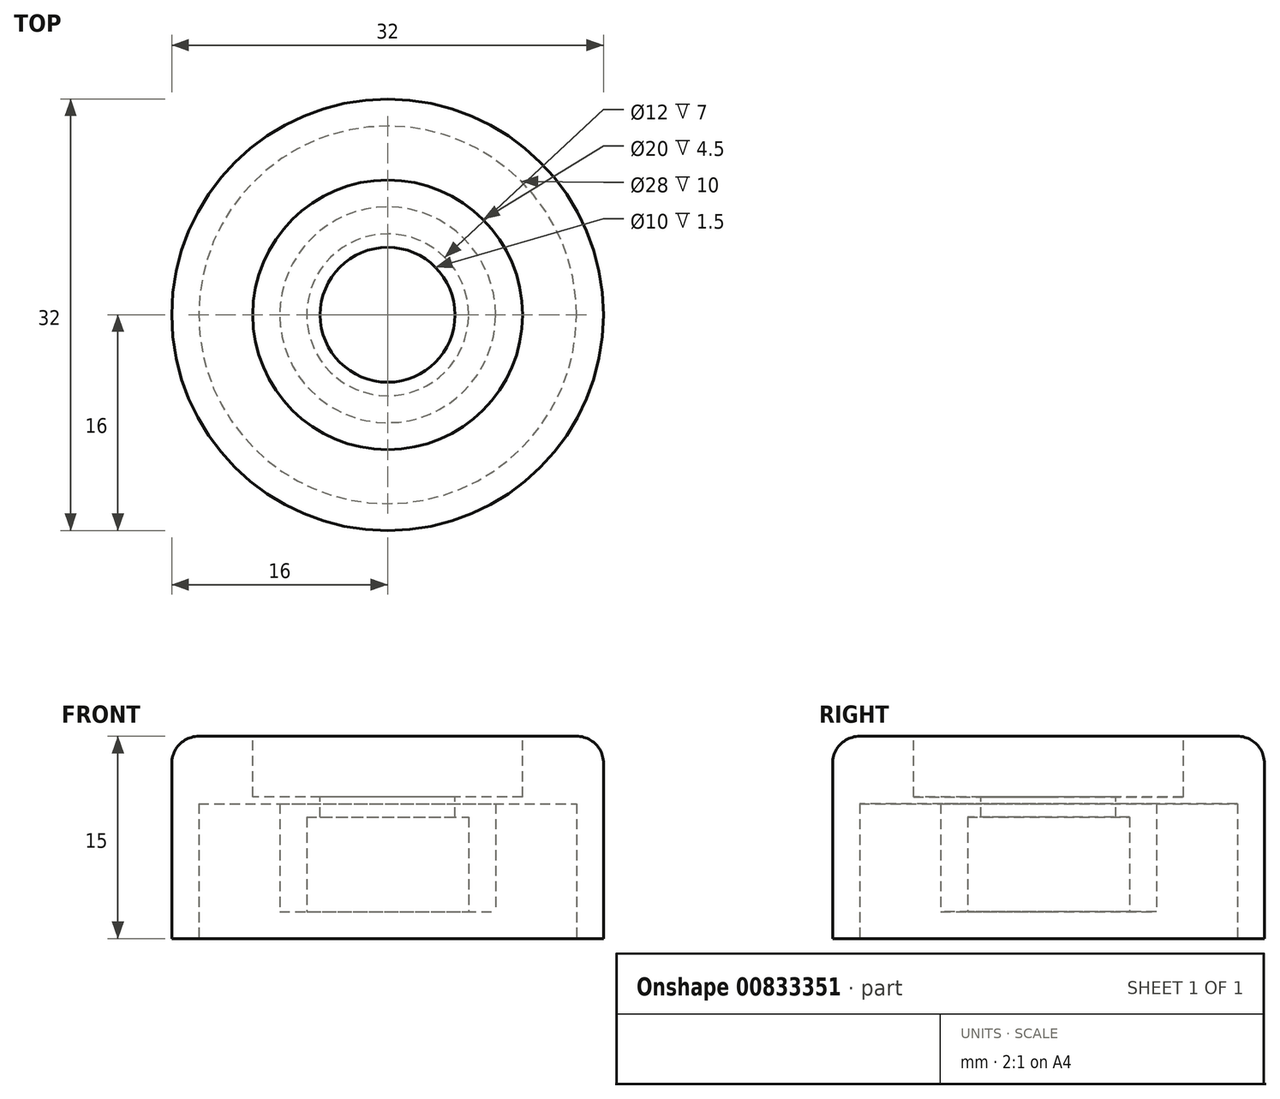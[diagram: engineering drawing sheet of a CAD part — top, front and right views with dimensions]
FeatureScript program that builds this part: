
annotation { "Feature Type Name" : "Feature", "Feature Type Description" : "" }
export const myFeature = defineFeature(function(context is Context, id is Id, definition is map)
    precondition{}
    {
        {
            var Q0;
            Q0=qCreatedBy(makeId("Top.planeOp"),FACE);
            var sketch = newSketch(context, id + "F0", { "sketchPlane" : qUnion([Q0])});
            skCircle(sketch, "E0", {"center": v(0, 0) * mm, "radius": 16 * mm});
            skSolve(sketch);
        }
        {
            var Q0;
            Q0=makeQuery(id+"F0.imprint","IMPRINT",FACE,{"disambiguationData":[TD([[makeQuery(id+"F0.imprint","IMPRINT",EDGE,{"derivedFrom":sQuery(id+"F0.wireOp",EDGE,"E0")}),1.0]])]});
            extrude(context, id + "F1", {"entities" : qUnion([Q0]), "depth" : 15 * mm, "offsetDistance" : 25 * mm});
        }
        {
            var Q0;
            Q0=makeQuery(id+"F1.opExtrude","CAP_FACE",FACE,{"disambiguationData":[OSD([sQuery(id+"F0.wireOp",EDGE,"E0")])],"isStart":false});
            var sketch = newSketch(context, id + "F2", { "sketchPlane" : qUnion([Q0])});
            skCircle(sketch, "E1", {"center": v(0, 0) * mm, "radius": 10 * mm});
            skSolve(sketch);
        }
        {
            var Q0;
            Q0=makeQuery(id+"F2.imprint","IMPRINT",FACE,{"disambiguationData":[TD([[makeQuery(id+"F2.imprint","IMPRINT",EDGE,{"derivedFrom":sQuery(id+"F2.wireOp",EDGE,"E1")}),1.0]])]});
            extrude(context, id + "F3", {"entities" : qUnion([Q0]), "operationType" : NewBodyOperationType.REMOVE, "oppositeDirection" : true, "depth" : 4.5 * mm, "offsetDistance" : 25 * mm});
        }
        {
            var Q0;
            Q0=makeQuery(id+"F1.opExtrude","CAP_FACE",FACE,{"disambiguationData":[OSD([sQuery(id+"F0.wireOp",EDGE,"E0")])],"isStart":true});
            var sketch = newSketch(context, id + "F4", { "sketchPlane" : qUnion([Q0])});
            skCircle(sketch, "E2", {"center": v(0, 0) * mm, "radius": 14 * mm});
            skCircle(sketch, "E3", {"center": v(0, 0) * mm, "radius": 6 * mm});
            skCircle(sketch, "E4", {"center": v(0, 0) * mm, "radius": 8 * mm});
            skSolve(sketch);
        }
        {
            var Q0;
            Q0=makeQuery(id+"F4.imprint","IMPRINT",FACE,{"disambiguationData":[TD([[makeQuery(id+"F4.imprint","IMPRINT",EDGE,{"derivedFrom":sQuery(id+"F4.wireOp",EDGE,"E2")}),1.0]])]});
            extrude(context, id + "F5", {"entities" : qUnion([Q0]), "operationType" : NewBodyOperationType.REMOVE, "oppositeDirection" : true, "depth" : 10 * mm, "offsetDistance" : 25 * mm});
        }
        {
            var Q0;
            Q0=makeQuery(id+"F5.boolean.opBoolean","SPLIT",FACE,{"disambiguationData":[TD([makeQuery(id+"F5.opExtrude","SWEPT_FACE",FACE,{"disambiguationData":[OSD([sQuery(id+"F4.wireOp",EDGE,"E4")])]})])],"derivedFrom":makeQuery(id+"F1.opExtrude","CAP_FACE",FACE,{"disambiguationData":[OSD([sQuery(id+"F0.wireOp",EDGE,"E0")])],"isStart":true})});
            var sketch = newSketch(context, id + "F6", { "sketchPlane" : qUnion([Q0])});
            skCircle(sketch, "E5", {"center": v(0, 0) * mm, "radius": 6 * mm});
            skSolve(sketch);
        }
        {
            var Q0;
            Q0=makeQuery(id+"F6.imprint","IMPRINT",FACE,{"disambiguationData":[TD([[makeQuery(id+"F6.imprint","IMPRINT",EDGE,{"derivedFrom":sQuery(id+"F6.wireOp",EDGE,"E5")}),1.0]])]});
            extrude(context, id + "F7", {"entities" : qUnion([Q0]), "operationType" : NewBodyOperationType.REMOVE, "oppositeDirection" : true, "depth" : 9 * mm, "offsetDistance" : 25 * mm});
        }
        {
            var Q0;
            Q0=makeQuery(id+"F3.boolean.opBoolean","COPY",FACE,{"derivedFrom":makeQuery(id+"F3.opExtrude","CAP_FACE",FACE,{"disambiguationData":[OSD([sQuery(id+"F2.wireOp",EDGE,"E1")])],"isStart":false})});
            var sketch = newSketch(context, id + "F8", { "sketchPlane" : qUnion([Q0])});
            skCircle(sketch, "E6", {"center": v(0, 0) * mm, "radius": 5 * mm});
            skSolve(sketch);
        }
        {
            var Q0;
            Q0=makeQuery(id+"F8.imprint","IMPRINT",FACE,{"disambiguationData":[TD([[makeQuery(id+"F8.imprint","IMPRINT",EDGE,{"derivedFrom":sQuery(id+"F8.wireOp",EDGE,"E6")}),1.0]])]});
            extrude(context, id + "F9", {"entities" : qUnion([Q0]), "operationType" : NewBodyOperationType.REMOVE, "oppositeDirection" : true, "depth" : 25 * mm, "offsetDistance" : 25 * mm});
        }
        {
            var Q0;
            Q0=makeQuery(id+"F5.boolean.opBoolean","SPLIT",FACE,{"disambiguationData":[TD([makeQuery(id+"F5.opExtrude","SWEPT_FACE",FACE,{"disambiguationData":[OSD([sQuery(id+"F4.wireOp",EDGE,"E4")])]})])],"derivedFrom":makeQuery(id+"F1.opExtrude","CAP_FACE",FACE,{"disambiguationData":[OSD([sQuery(id+"F0.wireOp",EDGE,"E0")])],"isStart":true})});
            var sketch = newSketch(context, id + "F10", { "sketchPlane" : qUnion([Q0])});
            skCircle(sketch, "E7", {"center": v(0, 0) * mm, "radius": 6 * mm});
            skCircle(sketch, "E8", {"center": v(0, 0) * mm, "radius": 8 * mm});
            skSolve(sketch);
        }
        {
            var Q0;
            Q0=makeQuery(id+"F10.imprint","IMPRINT",FACE,{"disambiguationData":[TD([[makeQuery(id+"F10.imprint","IMPRINT",EDGE,{"derivedFrom":sQuery(id+"F10.wireOp",EDGE,"E7")}),-1.0]])]});
            extrude(context, id + "F11", {"entities" : qUnion([Q0]), "operationType" : NewBodyOperationType.REMOVE, "oppositeDirection" : true, "depth" : 2 * mm, "offsetDistance" : 25 * mm});
        }
        {
            var Q0;
            Q0=makeQuery(id+"F1.opExtrude","CAP_EDGE",EDGE,{"disambiguationData":[OSD([sQuery(id+"F0.wireOp",EDGE,"E0")])],"isStart":false});
            var Q1;
            Q1=makeQuery(id+"F3.boolean.opBoolean","COPY",EDGE,{"derivedFrom":makeQuery(id+"F3.opExtrude","CAP_EDGE",EDGE,{"disambiguationData":[OSD([sQuery(id+"F2.wireOp",EDGE,"E1")])],"isStart":true})});
            fillet(context, id + "F12", {"entities" : qUnion([Q0, Q1]), "radius" : 2 * mm, "tangentPropagation" : true, "allowEdgeOverflow" : false});
        }
    });
